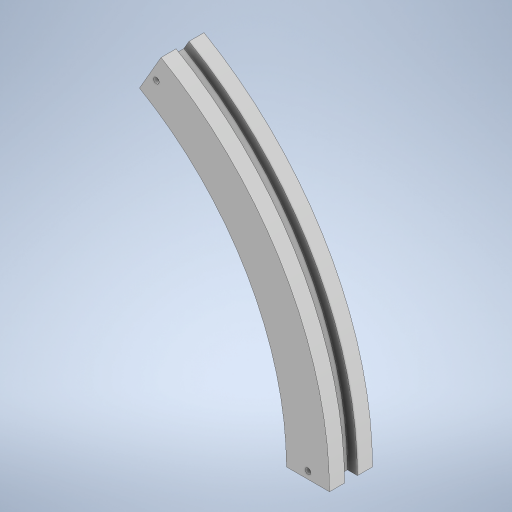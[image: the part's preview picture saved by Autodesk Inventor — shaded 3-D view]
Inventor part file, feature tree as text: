
AUTODESK INVENTOR PART (.ipt)
format: ipt  version: 2023 (Build 270158000, 158)  size: 356,864 bytes
history: native  units: mm
features: sketch x7, extrude x5, sweep x1
ambient origin geometry x8: Origin, YZ Plane, XZ Plane, XY Plane, X Axis, Y Axis, Z Axis, Center Point
bodies: Body1 (feature_tree)
feature tree (13):
  sweep  "Sweep2"
  extrude  "Extrusion3"  Depth=7.0mm
  extrude  "Extrusion5"  Depth=30.0mm
  extrude  "Extrusion6"  Depth=8.0mm
  extrude  "Extrusion7"  TaperAngle=60.0deg  [1 undecoded]
  extrude  "Extrusion8"  TaperAngle=0.0deg  [1 undecoded]
  sketch  "Sketch2"  dims[d5=100.0mm d18=9.0mm]
  sketch  "Sketch6"  dims[d19=7.0mm d21=16.0mm]
  sketch  "Sketch7"  dims[d22=30.0mm d23=15.0mm]
  sketch  "Sketch9"  dims[d24=4.5mm d25=8.0mm]
  sketch  "Sketch10"  dims[d41=220.0mm d42=60.0deg]
  sketch  "Sketch11"  dims[d43=220.0mm d44=0.0mm]
  sketch  "Sketch12"  dims[d45=0.0mm d46=0.0mm d47=2.5mm d48=2.5mm d49=2.5mm d50=2.5mm d51=2.5mm d52=2.5mm d53=2.5mm d54=2.5mm d55=2.5mm d56=10.0mm d57=0.0mm d63=4.0mm d65=5.0mm d66=15.0mm d67=0.0mm d68=0.0mm d69=2.5mm d70=2.5mm d71=2.5mm d72=2.5mm d73=2.5mm d74=2.5mm d75=2.5mm d76=2.5mm d77=10.0mm d78=0.0mm d79=4.0mm d80=5.0mm d81=15.0mm d82=0.0mm d83=0.0mm d85=239.167981mm d86=37.057395mm d87=18.642371mm d88=0.0mm d89=0.0mm d90=148.207407mm d91=115.0mm d92=181.651065mm]
note: 2 required parameter values undecoded (feature->parameter linkage not recoverable at this tier; creation-order binding heuristic only, values carry confidence <= 0.55)
